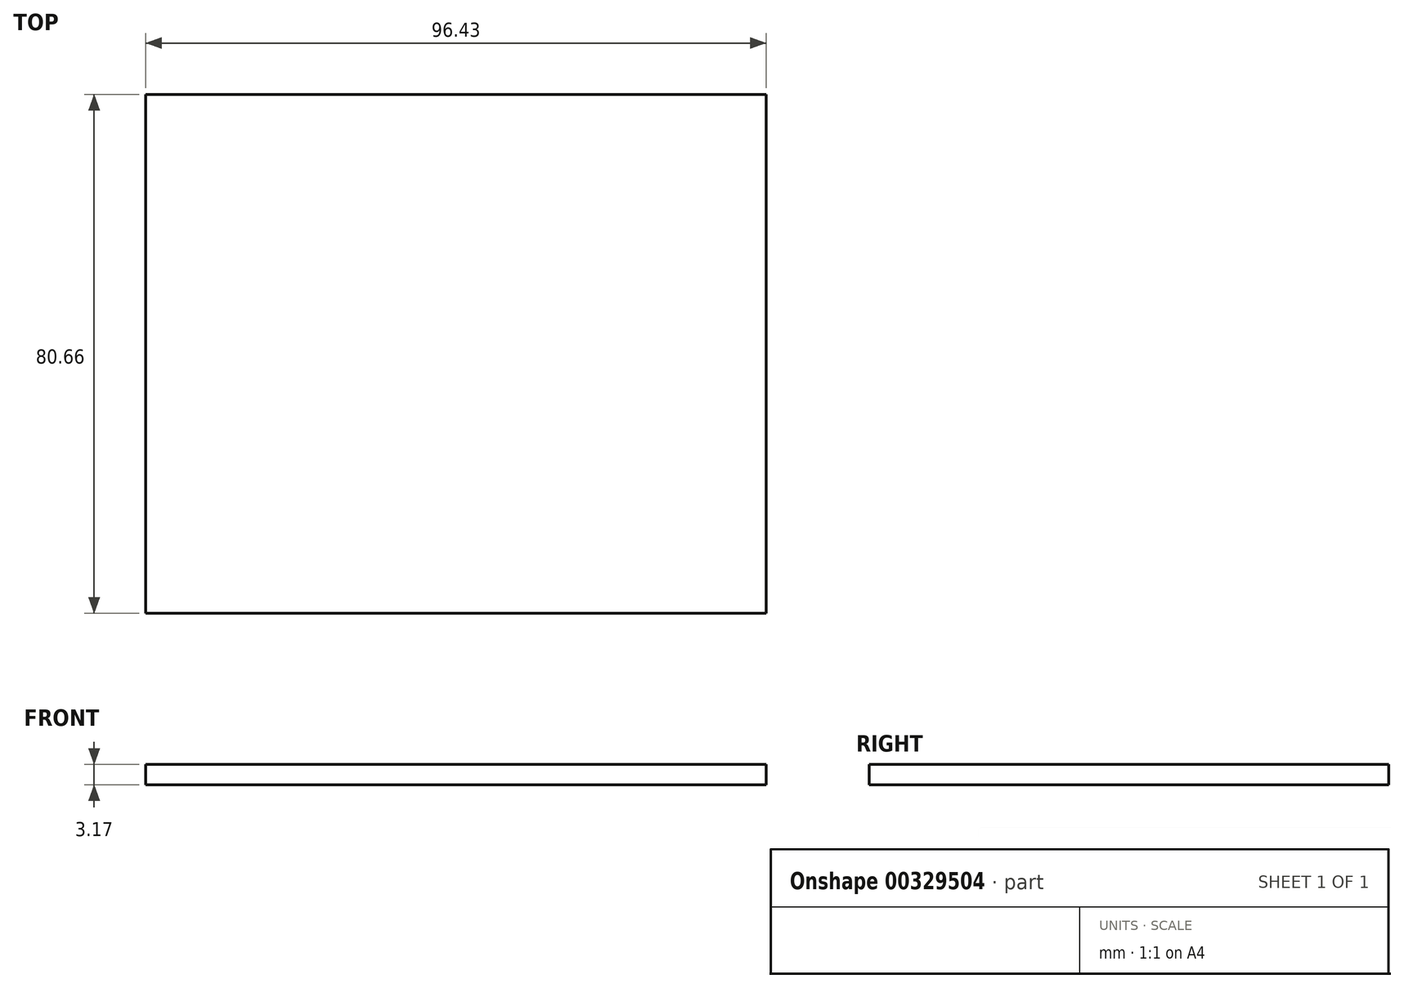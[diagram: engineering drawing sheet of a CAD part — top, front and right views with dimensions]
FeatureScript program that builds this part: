
annotation { "Feature Type Name" : "Feature", "Feature Type Description" : "" }
export const myFeature = defineFeature(function(context is Context, id is Id, definition is map)
    precondition{}
    {
        {
            var Q0;
            Q0=qCreatedBy(makeId("Top.planeOp"),FACE);
            var sketch = newSketch(context, id + "F0", { "sketchPlane" : qUnion([Q0])});
            skLineSegment(sketch, "E0.bottom", {"start": v(40.28, 49.04) * mm, "end": v(-56.15, 49.04) * mm});
            skLineSegment(sketch, "E0.top", {"start": v(40.28, -31.62) * mm, "end": v(-56.15, -31.62) * mm});
            skLineSegment(sketch, "E0.left", {"start": v(40.28, 49.04) * mm, "end": v(40.28, -31.62) * mm});
            skLineSegment(sketch, "E0.right", {"start": v(-56.15, 49.04) * mm, "end": v(-56.15, -31.62) * mm});
            skSolve(sketch);
        }
        {
            var Q0;
            Q0 = qSketchRegion(id + "F0", true);
            extrude(context, id + "F1", {"entities" : qUnion([Q0]), "depth" : 3.17 * mm});
        }
    });
